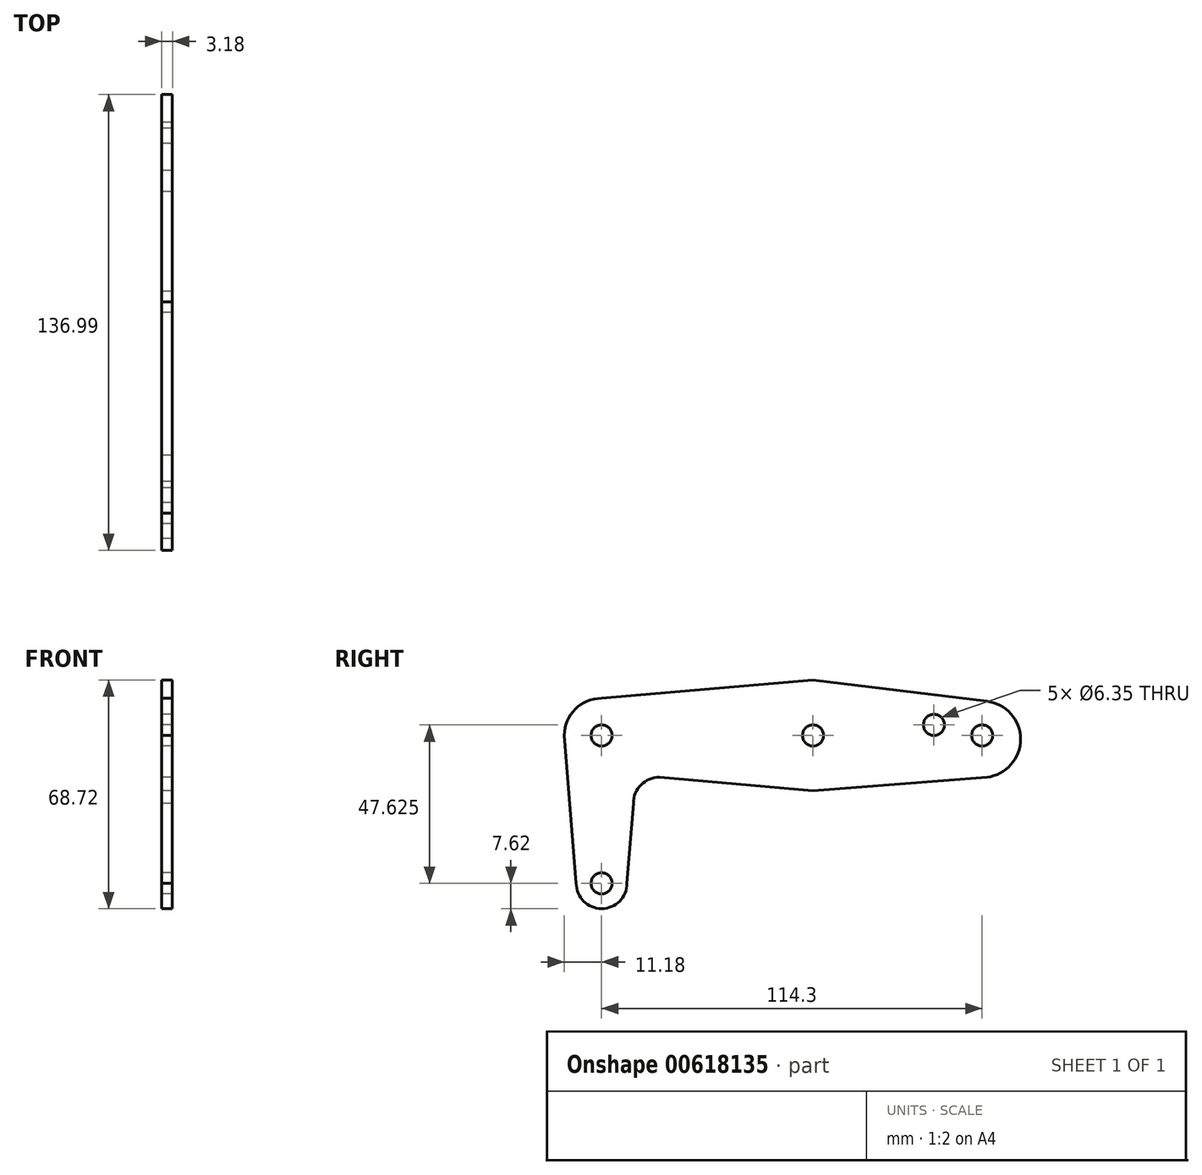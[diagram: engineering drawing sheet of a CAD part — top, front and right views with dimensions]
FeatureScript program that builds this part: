
annotation { "Feature Type Name" : "Feature", "Feature Type Description" : "" }
export const myFeature = defineFeature(function(context is Context, id is Id, definition is map)
    precondition{}
    {
        {
            var Q0;
            Q0=qCreatedBy(makeId("Right.planeOp"),FACE);
            var sketch = newSketch(context, id + "F0", { "sketchPlane" : qUnion([Q0])});
            skCircle(sketch, "E0", {"center": v(0, 0) * mm, "radius": 3.18 * mm});
            skArc(sketch, "E1", {"start": v(-7.62, 0) * mm, "mid": v(0, -7.62) * mm, "end": v(7.62, 0) * mm});
            skLineSegment(sketch, "E2", {"start": v(-7.62, 0) * mm, "end": v(-11.18, 44.45) * mm});
            skLineSegment(sketch, "E3", {"start": v(7.62, 0) * mm, "end": v(9.54, 24.03) * mm});
            skLineSegment(sketch, "E4", {"start": v(0, 0) * mm, "end": v(0, 44.45) * mm, "construction": true});
            skLineSegment(sketch, "E5", {"start": v(0, 44.45) * mm, "end": v(118.55, 44.45) * mm, "construction": true});
            skArc(sketch, "E6", {"start": v(-11.18, 44.45) * mm, "mid": v(-7.9, 52.35) * mm, "end": v(0, 55.63) * mm});
            skArc(sketch, "E7", {"start": v(9.54, 24.03) * mm, "mid": v(11.85, 29.6) * mm, "end": v(17.42, 31.9) * mm});
            skLineSegment(sketch, "E8", {"start": v(0, 55.63) * mm, "end": v(63.5, 61.1) * mm});
            skPoint(sketch, "E9.endSnap0", {"position": v(11.85, 29.6) * mm});
            skCircle(sketch, "E10", {"center": v(0, 44.45) * mm, "radius": 3.18 * mm});
            skCircle(sketch, "E11", {"center": v(114.3, 44.45) * mm, "radius": 3.18 * mm});
            skLineSegment(sketch, "E12", {"start": v(17.42, 31.9) * mm, "end": v(63.5, 27.81) * mm});
            skLineSegment(sketch, "E13", {"start": v(63.5, 27.81) * mm, "end": v(115.7, 31.9) * mm});
            skLineSegment(sketch, "E14", {"start": v(63.5, 61.1) * mm, "end": v(115.7, 54.74) * mm});
            skArc(sketch, "E15", {"start": v(115.7, 54.74) * mm, "mid": v(125.81, 43.32) * mm, "end": v(115.7, 31.9) * mm});
            skCircle(sketch, "E16", {"center": v(99.82, 47.62) * mm, "radius": 3.18 * mm});
            skCircle(sketch, "E17", {"center": v(63.5, 44.45) * mm, "radius": 3.18 * mm});
            skSolve(sketch);
        }
        {
            var Q0;
            Q0 = qSketchRegion(id + "F0", true);
            extrude(context, id + "F1", {"entities" : qUnion([Q0]), "depth" : 3.17 * mm, "offsetDistance" : 25.4 * mm});
        }
    });
